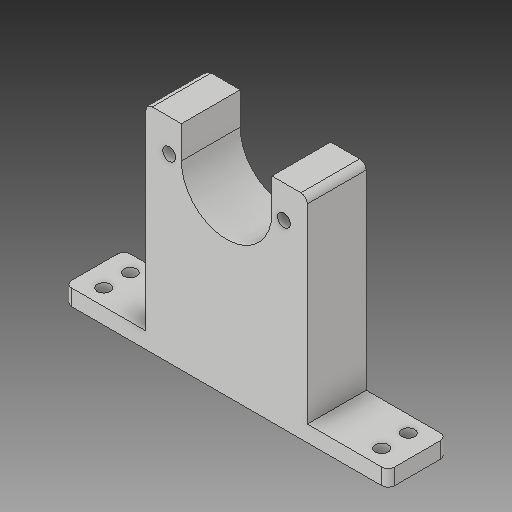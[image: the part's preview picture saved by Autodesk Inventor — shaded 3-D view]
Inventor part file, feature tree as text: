
AUTODESK INVENTOR PART (.ipt)
format: ipt  version: 2017 (Build 210142000, 142)  size: 159,232 bytes
history: native  units: mm
features: sketch x2, extrude x1, mirror x1, hole x1, fillet x1
ambient origin geometry x8: Origin, YZ Plane, XZ Plane, XY Plane, X Axis, Y Axis, Z Axis, Center Point
bodies: Solid1 (feature_tree)
feature tree (6):
  extrude  "Extrusion1"  Depth=50.0mm
  mirror  "Mirror1"
  hole  "Hole1"  [1 undecoded]
  fillet  "Fillet1"  Radius=14.0mm
  sketch  "Sketch1"  dims[d0=5.0mm d1=50.0mm]
  sketch  "Sketch2"  dims[d2=25.0mm d3=56.0mm d4=14.0mm d5=4.0mm d6=17.75mm d7=10.0mm d8=18.2mm d9=0.0mm d10=7.0mm d11=7.0mm d12=5.0mm d13=5.0mm d14=4.0mm d15=6.0mm d16=4.0mm d17=2.0mm d18=90.0deg d19=8.0mm d20=20.594885mm d21=2.0mm]
note: 1 required parameter value undecoded (feature->parameter linkage not recoverable at this tier; creation-order binding heuristic only, values carry confidence <= 0.55)
